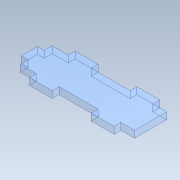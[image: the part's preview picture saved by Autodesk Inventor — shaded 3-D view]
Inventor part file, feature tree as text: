
AUTODESK INVENTOR PART (.ipt)
format: ipt  version: 2022 (Build 260153000, 153)  size: 302,592 bytes
history: native  units: mm
features: extrude x1, sketch x1
ambient origin geometry x8: Origin, YZ Plane, XZ Plane, XY Plane, X Axis, Y Axis, Z Axis, Center Point
bodies: Body1 (feature_tree)
feature tree (2):
  extrude  "Extrusion2"  [1 undecoded]
  sketch  "Sketch2"  dims[d3=3.0mm d4=0.0mm]
note: 1 required parameter value undecoded (feature->parameter linkage not recoverable at this tier; creation-order binding heuristic only, values carry confidence <= 0.55)
